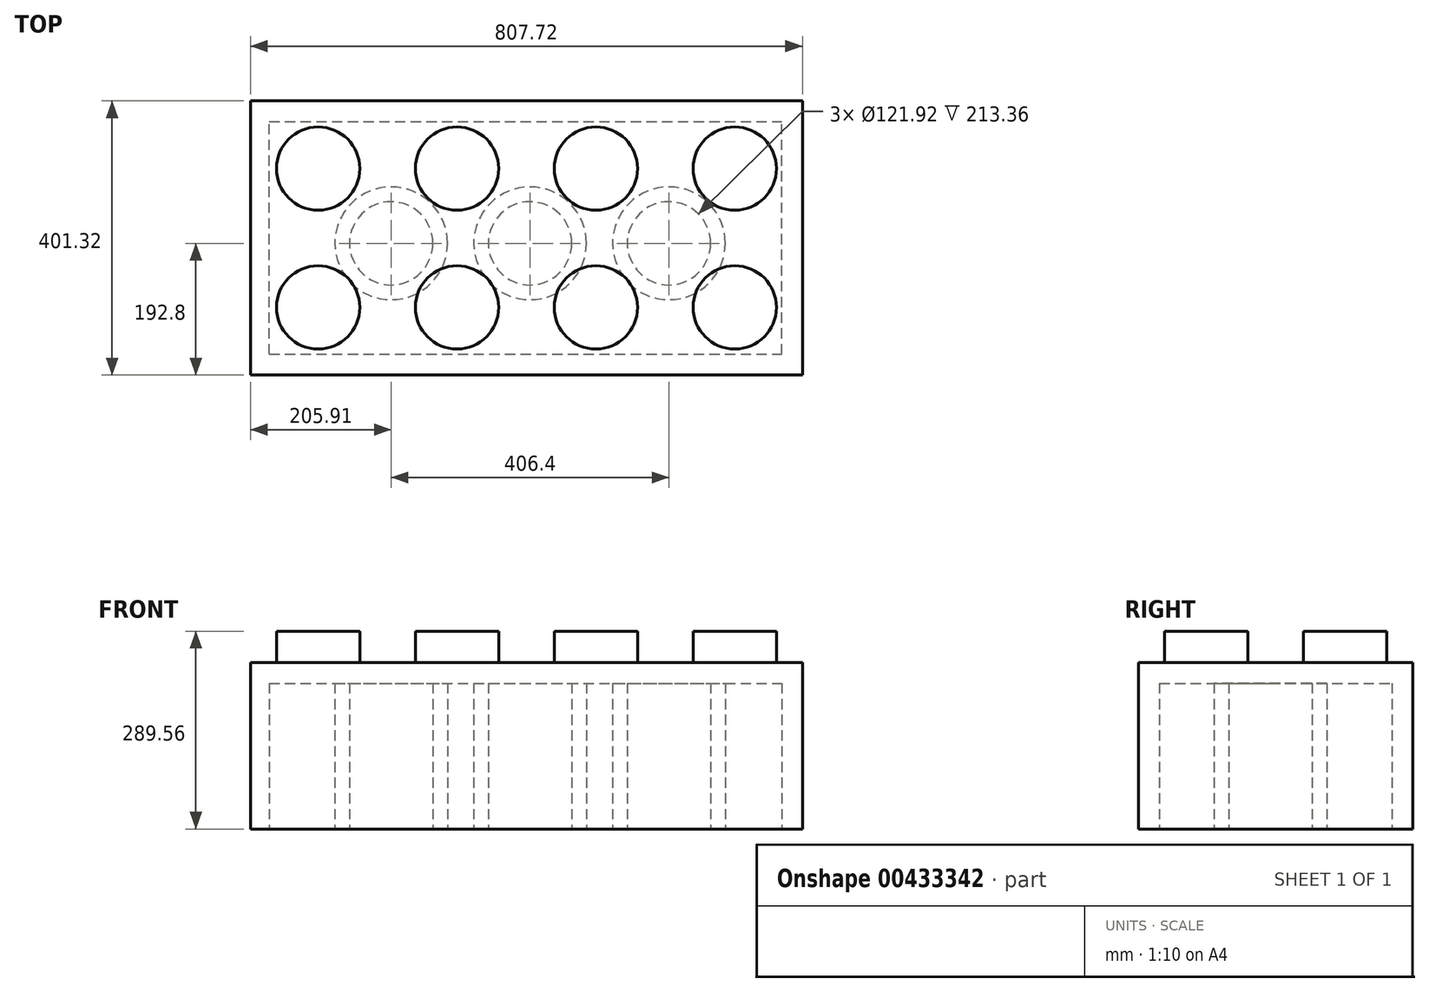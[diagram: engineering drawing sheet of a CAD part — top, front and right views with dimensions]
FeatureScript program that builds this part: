
annotation { "Feature Type Name" : "Feature", "Feature Type Description" : "" }
export const myFeature = defineFeature(function(context is Context, id is Id, definition is map)
    precondition{}
    {
        {
            var Q0;
            Q0=qCreatedBy(makeId("Top.planeOp"),FACE);
            var sketch = newSketch(context, id + "F0", { "sketchPlane" : qUnion([Q0])});
            skLineSegment(sketch, "E0.bottom", {"start": v(-409.11, 208.52) * mm, "end": v(398.6, 208.52) * mm});
            skLineSegment(sketch, "E0.top", {"start": v(-409.11, -192.8) * mm, "end": v(398.6, -192.8) * mm});
            skLineSegment(sketch, "E0.left", {"start": v(-409.11, 208.52) * mm, "end": v(-409.11, -192.8) * mm});
            skLineSegment(sketch, "E0.right", {"start": v(398.6, 208.52) * mm, "end": v(398.6, -192.8) * mm});
            skSolve(sketch);
        }
        {
            var Q0;
            Q0=makeQuery(id+"F0.imprint","IMPRINT",FACE,{"disambiguationData":[TD([[makeQuery(id+"F0.imprint","IMPRINT",EDGE,{"derivedFrom":sQuery(id+"F0.wireOp",EDGE,"E0.bottom")}),-1.0]])]});
            extrude(context, id + "F1", {"entities" : qUnion([Q0]), "depth" : 243.84 * mm});
        }
        {
            var Q0;
            Q0=makeQuery(id+"F1.opExtrude","CAP_FACE",FACE,{"disambiguationData":[OSD([sQuery(id+"F0.wireOp",EDGE,"E0.bottom"),sQuery(id+"F0.wireOp",EDGE,"E0.top"),sQuery(id+"F0.wireOp",EDGE,"E0.left"),sQuery(id+"F0.wireOp",EDGE,"E0.right")])],"isStart":false});
            var sketch = newSketch(context, id + "F2", { "sketchPlane" : qUnion([Q0])});
            skCircle(sketch, "E1", {"center": v(-310.05, 109.46) * mm, "radius": 60.96 * mm});
            skCircle(sketch, "E2.0.1.0", {"center": v(-310.05, -93.74) * mm, "radius": 60.96 * mm});
            skCircle(sketch, "E2.1.0.0", {"center": v(-106.85, 109.46) * mm, "radius": 60.96 * mm});
            skCircle(sketch, "E2.1.1.0", {"center": v(-106.85, -93.74) * mm, "radius": 60.96 * mm});
            skCircle(sketch, "E2.2.0.0", {"center": v(96.35, 109.46) * mm, "radius": 60.96 * mm});
            skCircle(sketch, "E2.2.1.0", {"center": v(96.35, -93.74) * mm, "radius": 60.96 * mm});
            skCircle(sketch, "E2.3.0.0", {"center": v(299.55, 109.46) * mm, "radius": 60.96 * mm});
            skCircle(sketch, "E2.3.1.0", {"center": v(299.55, -93.74) * mm, "radius": 60.96 * mm});
            skLineSegment(sketch, "E2.direction1", {"start": v(-310.05, 109.46) * mm, "end": v(-106.85, 109.46) * mm, "construction": true});
            skLineSegment(sketch, "E2.direction2", {"start": v(-310.05, 109.46) * mm, "end": v(-310.05, -93.74) * mm, "construction": true});
            skSolve(sketch);
        }
        {
            var Q0;
            Q0 = qSketchRegion(id + "F2", true);
            extrude(context, id + "F3", {"entities" : qUnion([Q0]), "operationType" : NewBodyOperationType.ADD, "depth" : 45.72 * mm});
        }
        {
            var Q0;
            Q0=makeQuery(id+"F1.opExtrude","CAP_FACE",FACE,{"disambiguationData":[OSD([sQuery(id+"F0.wireOp",EDGE,"E0.bottom"),sQuery(id+"F0.wireOp",EDGE,"E0.top"),sQuery(id+"F0.wireOp",EDGE,"E0.left"),sQuery(id+"F0.wireOp",EDGE,"E0.right")])],"isStart":true});
            var sketch = newSketch(context, id + "F4", { "sketchPlane" : qUnion([Q0])});
            skLineSegment(sketch, "E3.bottom", {"start": v(-381.68, 162.32) * mm, "end": v(368.13, 162.32) * mm});
            skLineSegment(sketch, "E3.top", {"start": v(-381.68, -178.04) * mm, "end": v(368.13, -178.04) * mm});
            skLineSegment(sketch, "E3.left", {"start": v(-381.68, 162.32) * mm, "end": v(-381.68, -178.04) * mm});
            skLineSegment(sketch, "E3.right", {"start": v(368.13, 162.32) * mm, "end": v(368.13, -178.04) * mm});
            skCircle(sketch, "E4", {"center": v(0, 0) * mm, "radius": 82.55 * mm});
            skCircle(sketch, "E5", {"center": v(0, 0) * mm, "radius": 60.96 * mm});
            skCircle(sketch, "E6.1.0.0", {"center": v(-203.2, 0) * mm, "radius": 60.96 * mm});
            skCircle(sketch, "E6.1.0.1", {"center": v(-203.2, 0) * mm, "radius": 82.55 * mm});
            skLineSegment(sketch, "E6.direction1", {"start": v(0, 0) * mm, "end": v(-203.2, 0) * mm, "construction": true});
            skCircle(sketch, "E7.1.0.0", {"center": v(203.2, 0) * mm, "radius": 60.96 * mm});
            skCircle(sketch, "E7.1.0.1", {"center": v(203.2, 0) * mm, "radius": 82.55 * mm});
            skLineSegment(sketch, "E7.direction1", {"start": v(0, 0) * mm, "end": v(203.2, 0) * mm, "construction": true});
            skSolve(sketch);
        }
        {
            var Q0;
            Q0=makeQuery(id+"F4.imprint","IMPRINT",FACE,{"disambiguationData":[TD([[makeQuery(id+"F4.imprint","IMPRINT",EDGE,{"derivedFrom":sQuery(id+"F4.wireOp",EDGE,"E3.bottom")}),-1.0]])]});
            var Q1;
            Q1=makeQuery(id+"F4.imprint","IMPRINT",FACE,{"disambiguationData":[TD([[makeQuery(id+"F4.imprint","IMPRINT",EDGE,{"derivedFrom":sQuery(id+"F4.wireOp",EDGE,"E6.1.0.0")}),1.0]])]});
            var Q2;
            Q2=makeQuery(id+"F4.imprint","IMPRINT",FACE,{"disambiguationData":[TD([[makeQuery(id+"F4.imprint","IMPRINT",EDGE,{"derivedFrom":sQuery(id+"F4.wireOp",EDGE,"E5")}),1.0]])]});
            var Q3;
            Q3=makeQuery(id+"F4.imprint","IMPRINT",FACE,{"disambiguationData":[TD([[makeQuery(id+"F4.imprint","IMPRINT",EDGE,{"derivedFrom":sQuery(id+"F4.wireOp",EDGE,"E7.1.0.0")}),1.0]])]});
            extrude(context, id + "F5", {"entities" : qUnion([Q0, Q1, Q2, Q3]), "operationType" : NewBodyOperationType.REMOVE, "oppositeDirection" : true, "depth" : 213.36 * mm});
        }
    });
